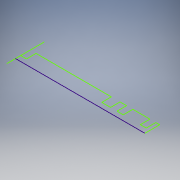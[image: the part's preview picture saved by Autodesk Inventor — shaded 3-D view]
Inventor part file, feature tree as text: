
AUTODESK INVENTOR PART (.ipt)
format: ipt  version: 2017 (Build 210142000, 142)  size: 87,552 bytes
history: native  units: mm
features: sketch x1
ambient origin geometry x8: Origin, YZ Plane, XZ Plane, XY Plane, X Axis, Y Axis, Z Axis, Center Point
feature tree (1):
  sketch  "Sketch1"
